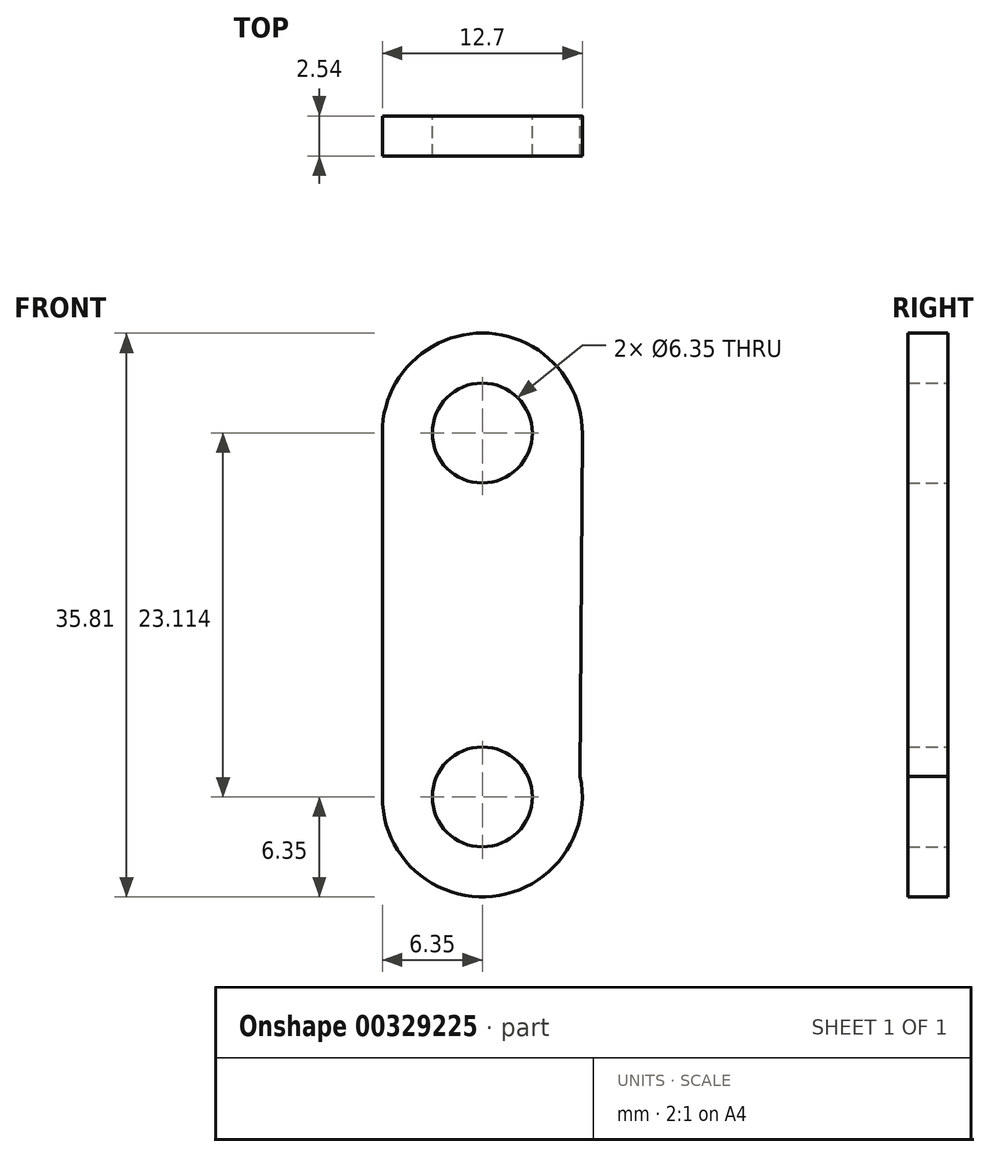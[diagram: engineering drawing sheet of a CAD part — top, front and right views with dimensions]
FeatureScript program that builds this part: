
annotation { "Feature Type Name" : "Feature", "Feature Type Description" : "" }
export const myFeature = defineFeature(function(context is Context, id is Id, definition is map)
    precondition{}
    {
        {
            var Q0;
            Q0=qCreatedBy(makeId("Front.planeOp"),FACE);
            var sketch = newSketch(context, id + "F0", { "sketchPlane" : qUnion([Q0])});
            skCircle(sketch, "E0", {"center": v(0, 0) * mm, "radius": 3.18 * mm});
            skCircle(sketch, "E1", {"center": v(0, 23.11) * mm, "radius": 6.35 * mm});
            skCircle(sketch, "E2", {"center": v(0, 23.11) * mm, "radius": 3.18 * mm});
            skCircle(sketch, "E3", {"center": v(0, 0) * mm, "radius": 6.35 * mm});
            skLineSegment(sketch, "E4", {"start": v(-6.35, 23.11) * mm, "end": v(-6.35, 0) * mm});
            skLineSegment(sketch, "E5", {"start": v(6.35, 23.07) * mm, "end": v(6.22, 1.3) * mm});
            skSolve(sketch);
        }
        {
            var Q0;
            Q0=makeQuery(id+"F0.imprint","IMPRINT",FACE,{"disambiguationData":[TD([[makeQuery(id+"F0.imprint","IMPRINT",EDGE,{"derivedFrom":sQuery(id+"F0.wireOp",EDGE,"E0")}),-1.0]])]});
            var Q1;
            {var subQ0=sQuery(id+"F0.wireOp",EDGE,"E4");Q1=makeQuery(id+"F0.imprint","IMPRINT",FACE,{"disambiguationData":[TD([[makeQuery(id+"F0.imprint","IMPRINT",EDGE,{"derivedFrom":subQ0}),1.0]])]});}
            var Q2;
            Q2=makeQuery(id+"F0.imprint","IMPRINT",FACE,{"disambiguationData":[TD([[makeQuery(id+"F0.imprint","IMPRINT",EDGE,{"derivedFrom":sQuery(id+"F0.wireOp",EDGE,"E2")}),-1.0]])]});
            extrude(context, id + "F1", {"entities" : qUnion([Q0, Q1, Q2]), "depth" : 2.54 * mm});
        }
    });
